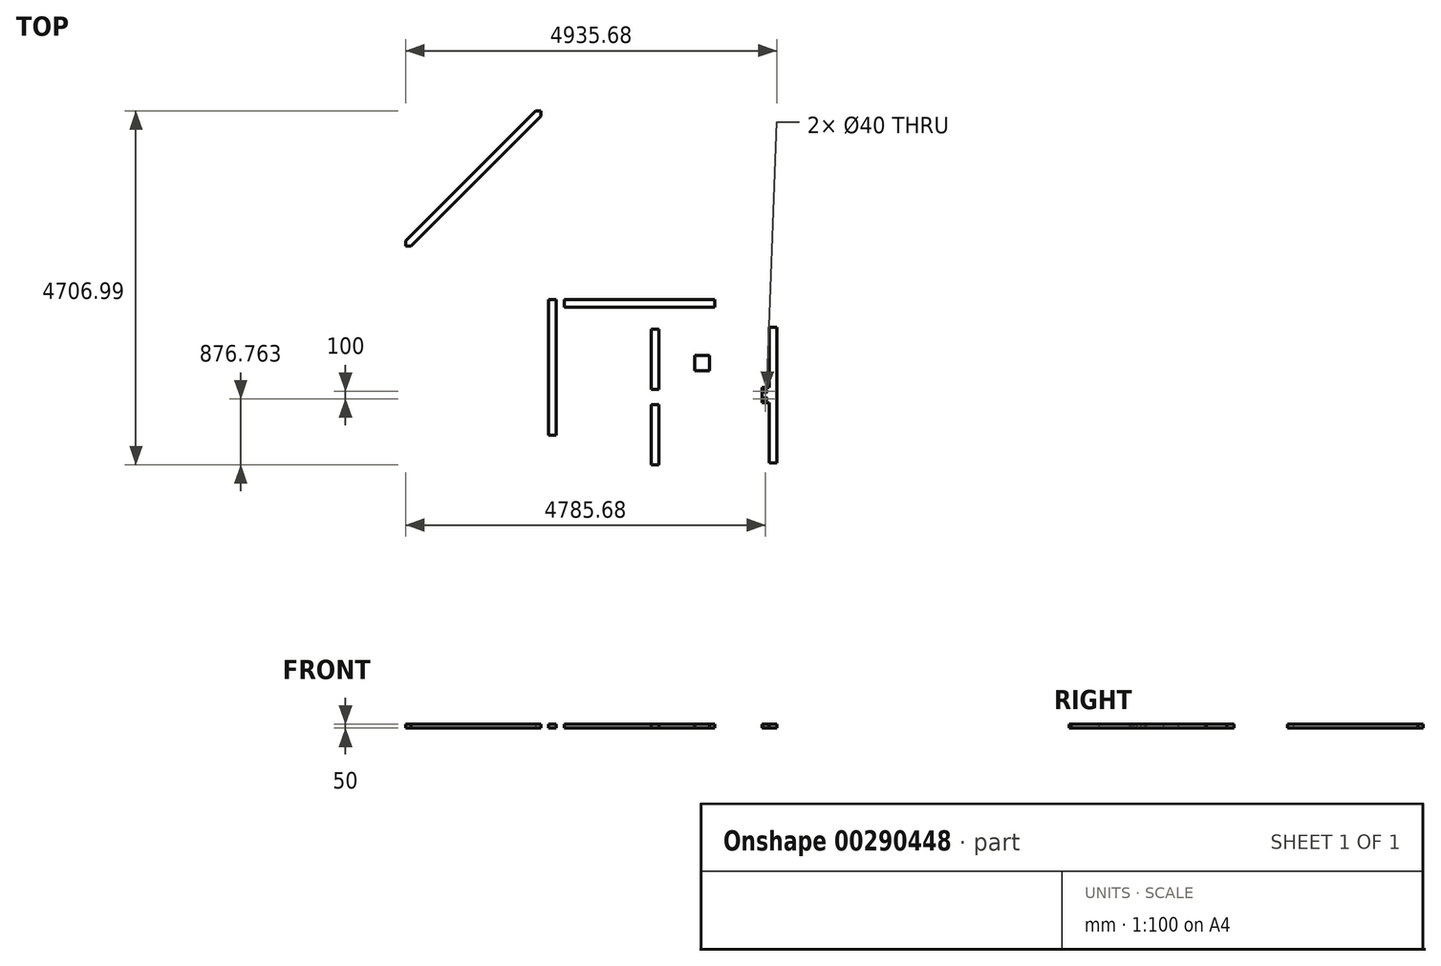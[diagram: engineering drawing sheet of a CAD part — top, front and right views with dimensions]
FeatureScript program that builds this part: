
annotation { "Feature Type Name" : "Feature", "Feature Type Description" : "" }
export const myFeature = defineFeature(function(context is Context, id is Id, definition is map)
    precondition{}
    {
        {
            var Q0;
            Q0=qCreatedBy(makeId("Top.planeOp"),FACE);
            var sketch = newSketch(context, id + "F0", { "sketchPlane" : qUnion([Q0])});
            skLineSegment(sketch, "E0.bottom", {"start": v(0, 0) * mm, "end": v(2000, 0) * mm});
            skLineSegment(sketch, "E0.top", {"start": v(0, -100) * mm, "end": v(2000, -100) * mm});
            skLineSegment(sketch, "E1.right", {"start": v(2000, -1900) * mm, "end": v(2000, -2000) * mm});
            skLineSegment(sketch, "E2.top", {"start": v(2000, -1900) * mm, "end": v(1900, -1900) * mm});
            skLineSegment(sketch, "E3", {"start": v(2000, 0) * mm, "end": v(2000, -100) * mm});
            skLineSegment(sketch, "E4", {"start": v(0, 0) * mm, "end": v(0, -100) * mm});
            skSolve(sketch);
        }
        {
            var Q0;
            Q0=makeQuery(id+"F0.imprint","IMPRINT",FACE,{"disambiguationData":[TD([[makeQuery(id+"F0.imprint","IMPRINT",EDGE,{"derivedFrom":sQuery(id+"F0.wireOp",EDGE,"IIBRwWCp-ZaJo-7xv1-Fq3U-lqCRKl8bDBzp.bottom")}),-1.0]])]});
            var Q1;
            Q1=makeQuery(id+"F0.imprint","IMPRINT",FACE,{"disambiguationData":[TD([[makeQuery(id+"F0.imprint","IMPRINT",EDGE,{"derivedFrom":sQuery(id+"F0.wireOp",EDGE,"E0.bottom")}),-1.0]])]});
            var Q2;
            Q2=makeQuery(id+"F0.imprint","IMPRINT",FACE,{"disambiguationData":[TD([[makeQuery(id+"F0.imprint","IMPRINT",EDGE,{"derivedFrom":sQuery(id+"F0.wireOp",EDGE,"E2.bottom")}),1.0]])]});
            var Q3;
            Q3=makeQuery(id+"F0.imprint","IMPRINT",FACE,{"disambiguationData":[TD([[makeQuery(id+"F0.imprint","IMPRINT",EDGE,{"derivedFrom":sQuery(id+"F0.wireOp",EDGE,"E1.top")}),1.0]])]});
            extrude(context, id + "F1", {"entities" : qUnion([Q0, Q1, Q2, Q3]), "depth" : 50 * mm});
        }
        {
            var Q0;
            Q0=qCreatedBy(makeId("Top.planeOp"),FACE);
            var sketch = newSketch(context, id + "F2", { "sketchPlane" : qUnion([Q0])});
            skLineSegment(sketch, "E5.bottom", {"start": v(-108.49, 0) * mm, "end": v(-208.49, 0) * mm});
            skLineSegment(sketch, "E5.top", {"start": v(-108.49, -1800) * mm, "end": v(-208.49, -1800) * mm});
            skLineSegment(sketch, "E5.left", {"start": v(-108.49, 0) * mm, "end": v(-108.49, -1800) * mm});
            skLineSegment(sketch, "E5.right", {"start": v(-208.49, 0) * mm, "end": v(-208.49, -1800) * mm});
            skSolve(sketch);
        }
        {
            var Q0;
            Q0=makeQuery(id+"F2.imprint","IMPRINT",FACE,{"disambiguationData":[TD([[makeQuery(id+"F2.imprint","IMPRINT",EDGE,{"derivedFrom":sQuery(id+"F2.wireOp",EDGE,"E5.bottom")}),1.0]])]});
            extrude(context, id + "F3", {"entities" : qUnion([Q0]), "depth" : 50 * mm});
        }
        {
            var Q0;
            Q0=qCreatedBy(makeId("Top.planeOp"),FACE);
            var sketch = newSketch(context, id + "F4", { "sketchPlane" : qUnion([Q0])});
            skLineSegment(sketch, "E6.bottom", {"start": v(1255.03, -395.2) * mm, "end": v(1155.03, -395.2) * mm});
            skLineSegment(sketch, "E6.top", {"start": v(1255.03, -2195.2) * mm, "end": v(1155.03, -2195.2) * mm});
            skLineSegment(sketch, "E7", {"start": v(1155.03, -1195.2) * mm, "end": v(1255.03, -1195.2) * mm});
            skLineSegment(sketch, "E8", {"start": v(1255.03, -1395.2) * mm, "end": v(1155.03, -1395.2) * mm});
            skLineSegment(sketch, "E9.left", {"start": v(1155.03, -2195.2) * mm, "end": v(1155.03, -1395.2) * mm});
            skLineSegment(sketch, "E9.right", {"start": v(1255.03, -2195.2) * mm, "end": v(1255.03, -1395.2) * mm});
            skLineSegment(sketch, "E10.left", {"start": v(1155.03, -395.2) * mm, "end": v(1155.03, -1195.2) * mm});
            skLineSegment(sketch, "E10.right", {"start": v(1255.03, -395.2) * mm, "end": v(1255.03, -1195.2) * mm});
            skSolve(sketch);
        }
        {
            var Q0;
            Q0 = qSketchRegion(id + "F4", true);
            extrude(context, id + "F5", {"entities" : qUnion([Q0]), "depth" : 50 * mm});
        }
        {
            var Q0;
            Q0=qCreatedBy(makeId("Top.planeOp"),FACE);
            var sketch = newSketch(context, id + "F6", { "sketchPlane" : qUnion([Q0])});
            skLineSegment(sketch, "E11.bottom", {"start": v(2826.13, -368.44) * mm, "end": v(2726.13, -368.44) * mm});
            skLineSegment(sketch, "E11.top", {"start": v(2826.13, -2168.44) * mm, "end": v(2726.13, -2168.44) * mm});
            skLineSegment(sketch, "E11.left", {"start": v(2826.13, -368.44) * mm, "end": v(2826.13, -2168.44) * mm});
            skLineSegment(sketch, "E12", {"start": v(2626.13, -1168.44) * mm, "end": v(2726.13, -1168.44) * mm});
            skLineSegment(sketch, "E13", {"start": v(2626.13, -1368.44) * mm, "end": v(2726.13, -1368.44) * mm});
            skLineSegment(sketch, "E14", {"start": v(2626.13, -1168.44) * mm, "end": v(2626.13, -1368.44) * mm});
            skLineSegment(sketch, "E15", {"start": v(2726.13, -1368.44) * mm, "end": v(2726.13, -2168.44) * mm});
            skLineSegment(sketch, "E16", {"start": v(2726.13, -1168.44) * mm, "end": v(2726.13, -368.44) * mm});
            skCircle(sketch, "E17", {"center": v(2676.13, -1218.44) * mm, "radius": 20 * mm});
            skCircle(sketch, "E18", {"center": v(2676.13, -1318.44) * mm, "radius": 20 * mm});
            skSolve(sketch);
        }
        {
            var Q0;
            Q0=makeQuery(id+"F6.imprint","IMPRINT",FACE,{"disambiguationData":[TD([[makeQuery(id+"F6.imprint","IMPRINT",EDGE,{"derivedFrom":sQuery(id+"F6.wireOp",EDGE,"E11.bottom")}),1.0]])]});
            extrude(context, id + "F7", {"entities" : qUnion([Q0]), "depth" : 50 * mm});
        }
        {
            var Q0;
            Q0=qCreatedBy(makeId("Top.planeOp"),FACE);
            var sketch = newSketch(context, id + "F8", { "sketchPlane" : qUnion([Q0])});
            skLineSegment(sketch, "E19", {"start": v(-309.55, 2441.08) * mm, "end": v(-309.55, 2511.79) * mm});
            skLineSegment(sketch, "E20", {"start": v(-309.55, 2511.79) * mm, "end": v(-380.26, 2511.79) * mm});
            skLineSegment(sketch, "E21", {"start": v(-380.26, 2511.79) * mm, "end": v(-2109.55, 782.5) * mm});
            skLineSegment(sketch, "E22", {"start": v(-2109.55, 782.5) * mm, "end": v(-2109.55, 711.79) * mm});
            skLineSegment(sketch, "E23", {"start": v(-2109.55, 711.79) * mm, "end": v(-2038.84, 711.79) * mm});
            skLineSegment(sketch, "E24", {"start": v(-2038.84, 711.79) * mm, "end": v(-309.55, 2441.08) * mm});
            skSolve(sketch);
        }
        {
            var Q0;
            Q0=makeQuery(id+"F8.imprint","IMPRINT",FACE,{"disambiguationData":[TD([[makeQuery(id+"F8.imprint","IMPRINT",EDGE,{"derivedFrom":sQuery(id+"F8.wireOp",EDGE,"E19")}),1.0]])]});
            extrude(context, id + "F9", {"entities" : qUnion([Q0]), "depth" : 50 * mm});
        }
        {
            var Q0;
            Q0=qCreatedBy(makeId("Top.planeOp"),FACE);
            var sketch = newSketch(context, id + "F10", { "sketchPlane" : qUnion([Q0])});
            skLineSegment(sketch, "E25.bottom", {"start": v(1732.35, -743.04) * mm, "end": v(1932.35, -743.04) * mm});
            skLineSegment(sketch, "E25.top", {"start": v(1732.35, -943.04) * mm, "end": v(1932.35, -943.04) * mm});
            skLineSegment(sketch, "E25.left", {"start": v(1732.35, -743.04) * mm, "end": v(1732.35, -943.04) * mm});
            skLineSegment(sketch, "E25.right", {"start": v(1932.35, -743.04) * mm, "end": v(1932.35, -943.04) * mm});
            skSolve(sketch);
        }
        {
            var Q0;
            Q0=makeQuery(id+"F10.imprint","IMPRINT",FACE,{"disambiguationData":[TD([[makeQuery(id+"F10.imprint","IMPRINT",EDGE,{"derivedFrom":sQuery(id+"F10.wireOp",EDGE,"E25.bottom")}),-1.0]])]});
            extrude(context, id + "F11", {"entities" : qUnion([Q0]), "depth" : 50 * mm});
        }
    });
